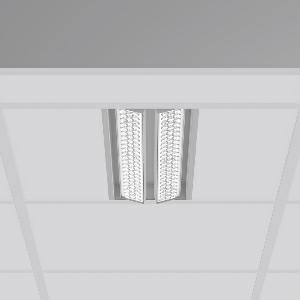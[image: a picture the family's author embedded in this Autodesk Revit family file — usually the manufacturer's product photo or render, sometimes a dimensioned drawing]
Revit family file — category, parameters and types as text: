
# Revit family: tx-move_901734_004_76_2ad2
name_source: partatom
category: Lighting Fixtures
units: mm (PartAtom-declared; Revit-internal decimal feet)

## family parameters
Cut with Voids When Loaded = No
Host = Face
Light Source = No
Part Type = Normal
Room Calculation Point = No
Round Connector Dimension = Use Diameter
Shared = No

## types (1)
- MultiLumen 1 (1 x LED Modul 830, 2625 lm, 3000)
    Apparent Load = 35 VA
    Approval mark = CE
    CIE Flux Codes = 65 90 98 100 100
    Color Rendering = 80
    Color Temperature = 3000
    Default Elevation = 1800 mm
    Description = Series: TX-MOVE
Einlege/Einbau-Flächenstrahler. Housing: sheet steel, powder-coated. 2xSwivel range: 90°. High-efficiency LED units with optimum light control thanks to clear plastic (PC) lens optics. Spezielle Mikrostrukturen reduzieren Gelbsaum. Asymmetrical light distribution. Suitable for laying in grid ceiling module 600. Connected converter included in separate gearbox.Suitable for through-wiring.MultiLumen: Luminous flux adjustable in 3 steps. Accessories: Mounting frame for installation in suspended ceilings. Environmentally friendly and resource-saving due to replaceable and recyclable components. 
Colour: silver, matt (approx. RAL 9006)
Length: 597 mm
Width: 190 mm
Height: 39 mm
Cut-out length: 577.5 mm
Cut-out width: 174 mm
Recess height: 100 mm
Lamp: LED
Socket: without socket
Colour temperature: 3000K
Colour rendering index (CRI): 80
System power: 35 W
Rated luminous flux: 5250 lm
Luminous efficiency: 150 lm/W
System power 2: 47 W
Rated luminous flux 2: 6800 lm
Luminous efficiency 2: 145 lm/W
System power 3: 68 W
Rated luminous flux 3: 9250 lm
Luminous efficiency 3: 136 lm/W
Control gear: Dimmable EVG, DALI
Protection class: I
Type of protection: IP 20
    Height = 0 mm  [stored 0 ft]
    Lamp = 1 x LED Modul 830
    Lamp Light Flux = 2625 lm
    Lamp count = 1
    Length = 597 mm
    Lifetime = 50000 h
    Luminous efficacy = 150 lm/W
    Manufacturer = RZB
    ModVariant = No
    Model = 901734.004.76
    Mounting Place = Ceiling, Wall
    Mounting Type = Recessed
    Number of Poles = 1
    OnlyDefault = Yes
    Power Factor = 1
    Product Name = TX-MOVE
    Product group = Recessed projectors
    ProductGroupID = 401
    Protection Class = Protection class I
    Protection Degree = IP 20
    RLX_Detail_Level = 1
    RLX_Emergency_Light_Flux = 0 lm
    RLX_Emergency_Type = 0
    RLX_Emergency_Type_DB = No
    RlxData = <blob elided: 56525 chars, md5=3d5d8f7c>
    Socket = socket
    Standby Power = 0 W
    System Light Flux = 5250 lm
    System Power = 35 W
    Type Comments = MultiLumen 1
    Type Image = 901733.004.jpg
    URL = http://relux.com
    VarID = multilumen_1
    Voltage = 230 V
    Voltage Range = 220-240 V
    Weight = 0.00 kg
    Width = 190 mm  [stored 0.62336 ft]

note: [stored X ft] marks values corroborated as IEEE doubles in the binary element streams (Revit-internal decimal feet)

## geometry (parser evidence)
native form markers: Blend x4, Sweep x16
no freeform markers — native parametric forms only
